# Revit family: Basin-Vanity_Sink-DXV-Belshire-D1908X030_Series
name_source: partatom
category: Plumbing Fixtures
units: mm (PartAtom-declared; Revit-internal decimal feet)

## family parameters
Always vertical = Yes
Cut with Voids When Loaded = No
OmniClass Number = 23.45.05.14.14
OmniClass Title = Sinks/Lavatories
Part Type = Normal
Room Calculation Point = No
Round Connector Dimension = Use Diameter
Shared = Yes
Work Plane-Based = No

## types (2) — shared parameters
Assembly Code = D2010400
Basin Shape = Rectangular
CW Connection = Yes
CWFU = 1.5
Cold Water Connection Diameter = 1/2"
Cold Water Connection Radius = 1/4"
Countertop Finish = Marble-DXV-550-Carrara
D20205000.415 Belshire rectangle under counter sink = Yes
HW Connection = Yes
HWFU = 1.5
Height = 36 3/16"
Hot Water Connection Diameter = 1/2"
Hot Water Connection Radius = 1/4"
Installation Type = Floor Mounted
Length = 22 1/2"
Manufacturer = DXV
Price = Prices may vary. Please consult Manufacturer Representative for most up-to-date price list.
Product Documentation Link = https://dxv01.blob.core.windows.net
Product Page URL = https://www.dxv.com
Revised Date = 04/05/2021
URL = https://www.dxv.com
Vent Connection = No
WFU = 2
Warranty Documentation Link = https://www.dxv.com
Waste Connection = Yes
Waste Connection Diameter = 1 1/4"
Width = 30"

## per-type parameters (varying)
| type | D19087000.150 Belshire vanity legs - Platinum Nickel | D19087000.427 Belshire vanity legs - Satin Brass | Description | Material | Vanity Finish | Vanity Leg Set Finish |
| D19085030.414 | Yes | No | DXV BELSHIRE™ NATURAL OAK VANITY | Wood_DXV-414-Natural_Oak | Wood_DXV-414-Natural_Oak | Metal-DXV-150-Platinum_Nickel |
| D19086030.326 | No | Yes | DXV BELSHIRE™ WALNUT OAK VANITY | Wood_DXV-329-Walnut | Wood_DXV-329-Walnut | Metal-DXV-427-Satin_Brass |

note: column(s) folded — value = type name in every type: Model

## geometry (parser evidence)
native form markers: Sweep x4
no freeform markers — native parametric forms only
